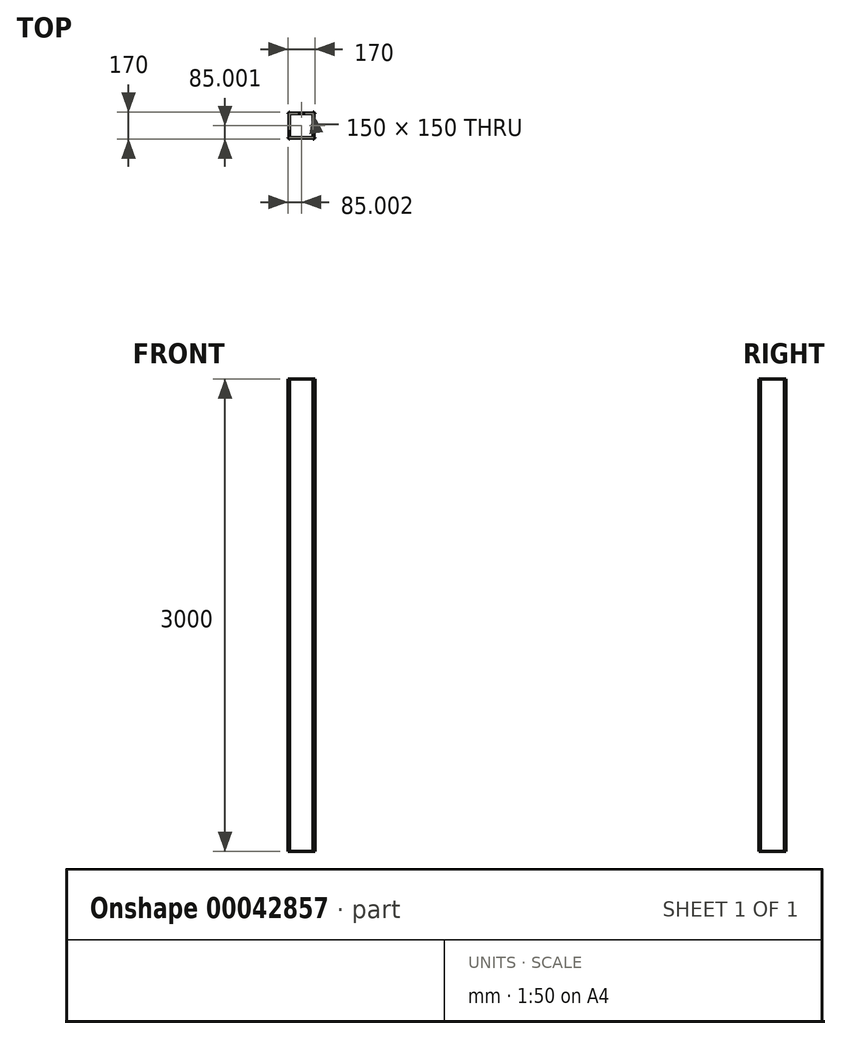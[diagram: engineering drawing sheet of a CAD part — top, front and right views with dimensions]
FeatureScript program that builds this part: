
annotation { "Feature Type Name" : "Feature", "Feature Type Description" : "" }
export const myFeature = defineFeature(function(context is Context, id is Id, definition is map)
    precondition{}
    {
        {
            var Q0;
            Q0=qCreatedBy(makeId("Top.planeOp"),FACE);
            var sketch = newSketch(context, id + "F0", { "sketchPlane" : qUnion([Q0])});
            skLineSegment(sketch, "E0", {"start": v(-86.73, 84) * mm, "end": v(-81.73, 84) * mm});
            skLineSegment(sketch, "E1", {"start": v(-81.73, 84) * mm, "end": v(-81.73, 89) * mm});
            skLineSegment(sketch, "E2", {"start": v(-81.73, 89) * mm, "end": v(-76.73, 89) * mm});
            skLineSegment(sketch, "E3", {"start": v(-76.73, 89) * mm, "end": v(-76.73, 84) * mm});
            skLineSegment(sketch, "E4", {"start": v(-76.73, 84) * mm, "end": v(73.27, 84) * mm});
            skLineSegment(sketch, "E5", {"start": v(73.27, 84) * mm, "end": v(73.27, 89) * mm});
            skLineSegment(sketch, "E6", {"start": v(73.27, 89) * mm, "end": v(78.27, 89) * mm});
            skLineSegment(sketch, "E7", {"start": v(78.27, 89) * mm, "end": v(78.27, 84) * mm});
            skLineSegment(sketch, "E8", {"start": v(78.27, 84) * mm, "end": v(83.27, 84) * mm});
            skLineSegment(sketch, "E9", {"start": v(83.27, 84) * mm, "end": v(83.27, 79) * mm});
            skLineSegment(sketch, "E10", {"start": v(83.27, 79) * mm, "end": v(78.27, 79) * mm});
            skLineSegment(sketch, "E11", {"start": v(78.27, 79) * mm, "end": v(78.27, -71) * mm});
            skLineSegment(sketch, "E12", {"start": v(78.27, -71) * mm, "end": v(83.27, -71) * mm});
            skLineSegment(sketch, "E13", {"start": v(83.27, -71) * mm, "end": v(83.27, -76) * mm});
            skLineSegment(sketch, "E14", {"start": v(83.27, -76) * mm, "end": v(78.27, -76) * mm});
            skLineSegment(sketch, "E15", {"start": v(78.27, -76) * mm, "end": v(78.27, -81) * mm});
            skLineSegment(sketch, "E16", {"start": v(78.27, -81) * mm, "end": v(73.27, -81) * mm});
            skLineSegment(sketch, "E17", {"start": v(73.27, -81) * mm, "end": v(73.27, -76) * mm});
            skLineSegment(sketch, "E18", {"start": v(73.27, -76) * mm, "end": v(-76.73, -76) * mm});
            skLineSegment(sketch, "E19", {"start": v(-76.73, -76) * mm, "end": v(-76.73, -81) * mm});
            skLineSegment(sketch, "E20", {"start": v(-76.73, -81) * mm, "end": v(-81.73, -81) * mm});
            skLineSegment(sketch, "E21", {"start": v(-81.73, -81) * mm, "end": v(-81.73, -76) * mm});
            skLineSegment(sketch, "E22", {"start": v(-81.73, -76) * mm, "end": v(-86.73, -76) * mm});
            skLineSegment(sketch, "E23", {"start": v(-86.73, -76) * mm, "end": v(-86.73, -71) * mm});
            skLineSegment(sketch, "E24", {"start": v(-86.73, -71) * mm, "end": v(-81.73, -71) * mm});
            skLineSegment(sketch, "E25", {"start": v(-81.73, -71) * mm, "end": v(-81.73, 79) * mm});
            skLineSegment(sketch, "E26", {"start": v(-81.73, 79) * mm, "end": v(-86.73, 79) * mm});
            skLineSegment(sketch, "E27", {"start": v(-86.73, 79) * mm, "end": v(-86.73, 84) * mm});
            skLineSegment(sketch, "E28.bottom", {"start": v(-76.73, 79) * mm, "end": v(73.27, 79) * mm});
            skLineSegment(sketch, "E28.top", {"start": v(-76.73, -71) * mm, "end": v(73.27, -71) * mm});
            skLineSegment(sketch, "E28.left", {"start": v(-76.73, 79) * mm, "end": v(-76.73, -71) * mm});
            skLineSegment(sketch, "E28.right", {"start": v(73.27, 79) * mm, "end": v(73.27, -71) * mm});
            skSolve(sketch);
        }
        {
            var Q0;
            Q0=makeQuery(id+"F0.imprint","IMPRINT",FACE,{"disambiguationData":[TD([[makeQuery(id+"F0.imprint","IMPRINT",EDGE,{"derivedFrom":sQuery(id+"F0.wireOp",EDGE,"E0")}),-1.0]])]});
            extrude(context, id + "F1", {"entities" : qUnion([Q0]), "depth" : 3000 * mm});
        }
    });
